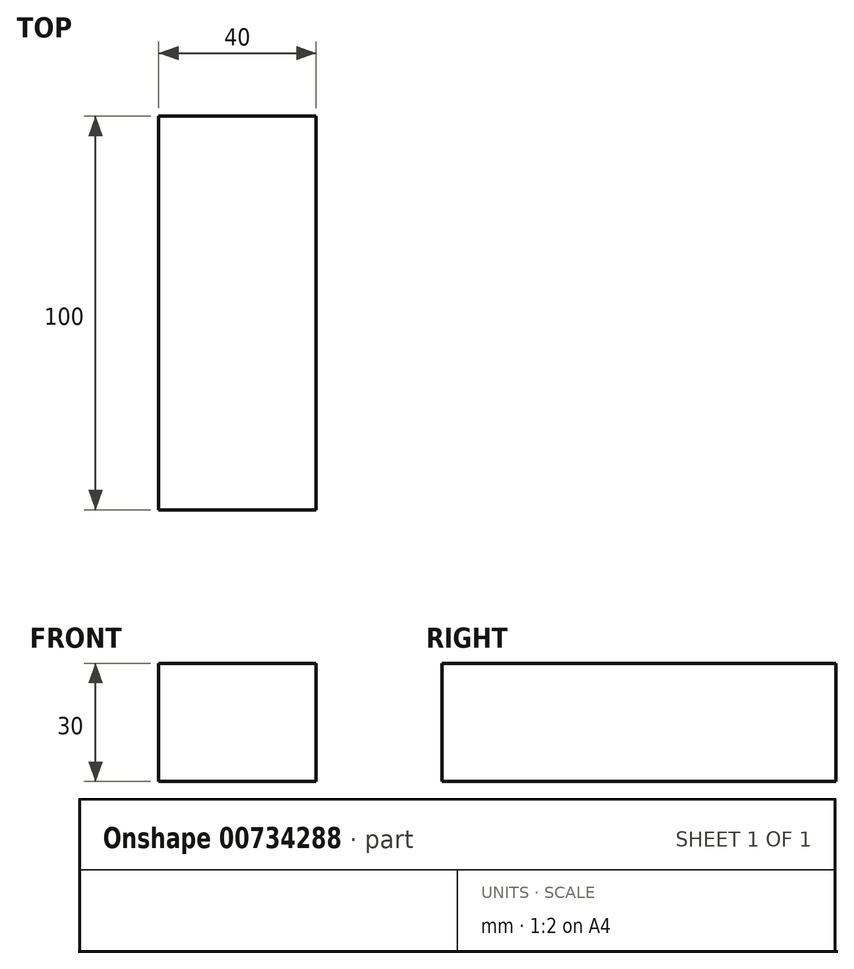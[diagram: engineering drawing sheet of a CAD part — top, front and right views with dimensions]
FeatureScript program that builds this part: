
annotation { "Feature Type Name" : "Feature", "Feature Type Description" : "" }
export const myFeature = defineFeature(function(context is Context, id is Id, definition is map)
    precondition{}
    {
        {
            var Q0;
            Q0=qCreatedBy(makeId("Front.planeOp"),FACE);
            var sketch = newSketch(context, id + "F0", { "sketchPlane" : qUnion([Q0])});
            skLineSegment(sketch, "E0.bottom", {"start": v(0, 0) * mm, "end": v(40, 0) * mm});
            skLineSegment(sketch, "E0.top", {"start": v(0, 30) * mm, "end": v(40, 30) * mm});
            skLineSegment(sketch, "E0.left", {"start": v(0, 0) * mm, "end": v(0, 30) * mm});
            skLineSegment(sketch, "E0.right", {"start": v(40, 0) * mm, "end": v(40, 30) * mm});
            skSolve(sketch);
        }
        {
            var Q0;
            Q0 = qSketchRegion(id + "F0", true);
            extrude(context, id + "F1", {"entities" : qUnion([Q0]), "depth" : 100 * mm, "offsetDistance" : 25 * mm});
        }
    });
